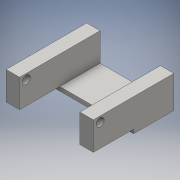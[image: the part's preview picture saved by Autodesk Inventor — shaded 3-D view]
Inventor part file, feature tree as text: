
AUTODESK INVENTOR PART (.ipt)
format: ipt  version: 2016 (Build 200138000, 138)  size: 117,248 bytes
history: native  units: mm
features: extrude x3, sketch x3, other x1
ambient origin geometry x8: Origin, YZ Plane, XZ Plane, XY Plane, X Axis, Y Axis, Z Axis, Center Point
bodies: Body1 (feature_tree)
feature tree (7):
  other  "ソリッド1"
  extrude  "押し出し1"  Depth=30.0mm
  extrude  "押し出し2"  Depth=65.0mm
  extrude  "押し出し3"  Depth=3.0mm TaperAngle=0.0deg
  sketch  "スケッチ1"
  sketch  "スケッチ2"
  sketch  "スケッチ3"
